# Revit family: LLIFE-PRO-SPOT-SMS R14
name_source: partatom
category: Lighting Fixtures
revit_build: Autodesk Revit 2015 (Build: 20140606_1530(x64)
units: mm (PartAtom-declared; Revit-internal decimal feet)

## types (1)
- LLIFE-PRO-SPOT-SMS-DALI
    1100830 = 2 X 3W LED Round Head Assembly - White
    1530230 = Battery, 3.3V 5Ah.Li-ion, 200mm lead with Bracket
    8002200 = DALI Node
    8002390 = Driver, PCA:Lifelight Pro, Aoneworks Compatible
    Catalogue Number = LLIFE-PRO-SPOT-SMS-DALI
    Charging Method = Intelligent current limited constant voltage charger
    Description1 = Lifelight PRO, High Performance, Surface Mount Emergency Spotlight with Lithium Battery Technology
    Height = 60 mm
    IP Rating = IP20
    Lamp = 2 X 3W LED (Lifetime warranty on the lamp head and loom assembly) No dome cover required
    Lamp head and swivel assembly = 105 mm
    Length = 267 mm
    Mounting = Surface Mounting
    Operating Mode = Non-Maintained
    Operating Temperature = 1°C to 40°C (Ambient)
    Operating Voltage = 240V 50Hz
    Power Consumption = 0.4 Watts
    Testing System = DALI Compatible
    Width = 148 mm

## geometry (parser evidence)
native form markers: Sweep x20
no freeform markers — native parametric forms only
